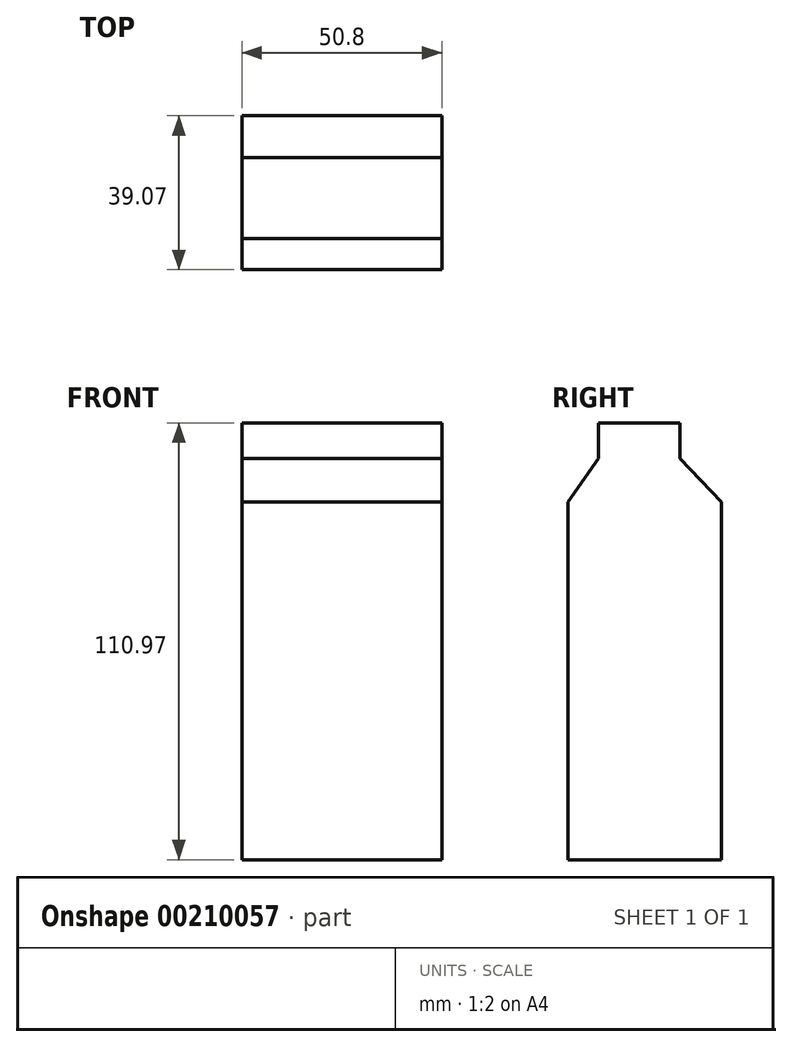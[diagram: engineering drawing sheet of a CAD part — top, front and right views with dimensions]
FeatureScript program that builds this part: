
annotation { "Feature Type Name" : "Feature", "Feature Type Description" : "" }
export const myFeature = defineFeature(function(context is Context, id is Id, definition is map)
    precondition{}
    {
        {
            var Q0;
            Q0=qCreatedBy(makeId("Right.planeOp"),FACE);
            var sketch = newSketch(context, id + "F0", { "sketchPlane" : qUnion([Q0])});
            skLineSegment(sketch, "E0", {"start": v(0, 52.67) * mm, "end": v(9.53, 52.67) * mm});
            skLineSegment(sketch, "E1", {"start": v(9.53, 52.67) * mm, "end": v(9.53, 43.6) * mm});
            skLineSegment(sketch, "E2", {"start": v(9.53, 43.6) * mm, "end": v(20.16, 32.66) * mm});
            skLineSegment(sketch, "E3", {"start": v(20.16, 32.66) * mm, "end": v(20.16, -58.3) * mm});
            skLineSegment(sketch, "E4", {"start": v(20.16, -58.3) * mm, "end": v(0, -58.3) * mm});
            skLineSegment(sketch, "E5", {"start": v(0, -58.3) * mm, "end": v(-18.91, -58.3) * mm});
            skLineSegment(sketch, "E6", {"start": v(-18.91, -58.3) * mm, "end": v(-18.91, 32.66) * mm});
            skLineSegment(sketch, "E7", {"start": v(0, 52.67) * mm, "end": v(-11.1, 52.67) * mm});
            skLineSegment(sketch, "E8", {"start": v(-11.1, 52.67) * mm, "end": v(-11.1, 43.6) * mm});
            skLineSegment(sketch, "E9", {"start": v(-11.1, 43.6) * mm, "end": v(-18.91, 32.66) * mm});
            skLineSegment(sketch, "E10", {"start": v(-11.1, 43.6) * mm, "end": v(9.53, 43.6) * mm});
            skSolve(sketch);
        }
        {
            var Q0;
            Q0=makeQuery(id+"F0.imprint","IMPRINT",FACE,{"disambiguationData":[TD([[makeQuery(id+"F0.imprint","IMPRINT",EDGE,{"derivedFrom":sQuery(id+"F0.wireOp",EDGE,"E0")}),-1.0]])]});
            var Q1;
            Q1=makeQuery(id+"F0.imprint","IMPRINT",FACE,{"disambiguationData":[TD([[makeQuery(id+"F0.imprint","IMPRINT",EDGE,{"derivedFrom":sQuery(id+"F0.wireOp",EDGE,"E2")}),-1.0]])]});
            extrude(context, id + "F1", {"entities" : qUnion([Q0, Q1]), "depth" : 25.4 * mm});
        }
        {
            var Q0;
            Q0=makeQuery(id+"F1.opExtrude","CAP_FACE",FACE,{"disambiguationData":[OSD([sQuery(id+"F0.wireOp",EDGE,"E0"),sQuery(id+"F0.wireOp",EDGE,"E1"),sQuery(id+"F0.wireOp",EDGE,"E2"),sQuery(id+"F0.wireOp",EDGE,"E3"),sQuery(id+"F0.wireOp",EDGE,"E4"),sQuery(id+"F0.wireOp",EDGE,"E5"),sQuery(id+"F0.wireOp",EDGE,"E6"),sQuery(id+"F0.wireOp",EDGE,"E7"),sQuery(id+"F0.wireOp",EDGE,"E8"),sQuery(id+"F0.wireOp",EDGE,"E9")])],"isStart":true});
            extrude(context, id + "F2", {"entities" : qUnion([Q0]), "operationType" : NewBodyOperationType.ADD, "depth" : 25.4 * mm});
        }
    });
